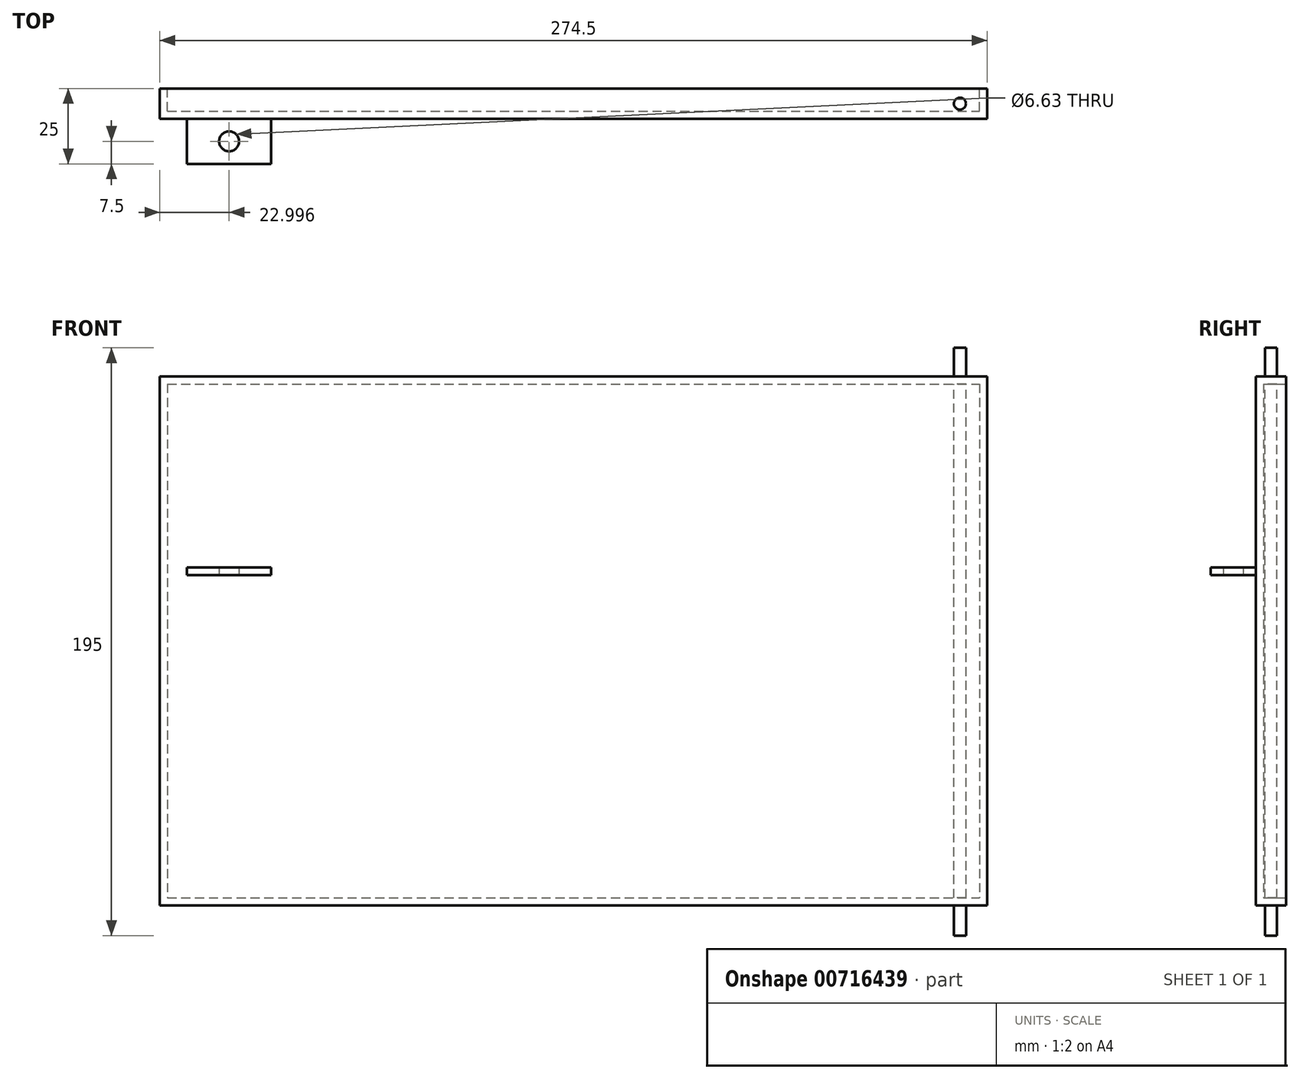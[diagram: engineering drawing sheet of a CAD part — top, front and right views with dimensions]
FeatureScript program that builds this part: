
annotation { "Feature Type Name" : "Feature", "Feature Type Description" : "" }
export const myFeature = defineFeature(function(context is Context, id is Id, definition is map)
    precondition{}
    {
        {
            var Q0;
            Q0=qCreatedBy(makeId("Top.planeOp"),FACE);
            var sketch = newSketch(context, id + "F0", { "sketchPlane" : qUnion([Q0])});
            skLineSegment(sketch, "E0.bottom", {"start": v(0, 0) * mm, "end": v(274.5, 0) * mm});
            skLineSegment(sketch, "E0.top", {"start": v(0, 10) * mm, "end": v(274.5, 10) * mm});
            skLineSegment(sketch, "E0.left", {"start": v(0, 0) * mm, "end": v(0, 10) * mm});
            skLineSegment(sketch, "E0.right", {"start": v(274.5, 0) * mm, "end": v(274.5, 10) * mm});
            skSolve(sketch);
        }
        {
            var Q0;
            Q0=qSketchRegion(id+"F0",true);
            extrude(context, id + "F1", {"entities" : qUnion([Q0]), "depth" : 175.5 * mm, "offsetDistance" : 25 * mm});
        }
        {
            var Q0;
            Q0=makeQuery(id+"F1.opExtrude","SWEPT_FACE",FACE,{"disambiguationData":[OSD([sQuery(id+"F0.wireOp",EDGE,"E0.top")])]});
            shell(context, id + "F2", {"entities" : qUnion([Q0]), "thickness" : 2.5 * mm});
        }
        {
            var Q0;
            Q0=makeQuery(id+"F1.opExtrude","CAP_FACE",FACE,{"disambiguationData":[OSD([sQuery(id+"F0.wireOp",EDGE,"E0.bottom"),sQuery(id+"F0.wireOp",EDGE,"E0.top"),sQuery(id+"F0.wireOp",EDGE,"E0.left"),sQuery(id+"F0.wireOp",EDGE,"E0.right")])],"isStart":true});
            var sketch = newSketch(context, id + "F3", { "sketchPlane" : qUnion([Q0])});
            skCircle(sketch, "E1", {"center": v(265.5, -5) * mm, "radius": 2 * mm});
            skPoint(sketch, "E1.centerSnap0", {"position": v(274.5, -5) * mm});
            skSolve(sketch);
        }
        {
            var Q0;
            Q0=qSketchRegion(id+"F3",true);
            extrude(context, id + "F4", {"entities" : qUnion([Q0]), "operationType" : NewBodyOperationType.ADD, "depth" : 10 * mm, "offsetDistance" : 25 * mm, "hasSecondDirection" : true, "secondDirectionOppositeDirection" : true, "secondDirectionDepth" : 185 * mm});
        }
        {
            var Q0;
            Q0=makeQuery(id+"F1.opExtrude","SWEPT_FACE",FACE,{"disambiguationData":[OSD([sQuery(id+"F0.wireOp",EDGE,"E0.bottom")])]});
            var sketch = newSketch(context, id + "F5", { "sketchPlane" : qUnion([Q0])});
            skLineSegment(sketch, "E2.bottom", {"start": v(9.05, 109.64) * mm, "end": v(36.95, 109.64) * mm});
            skLineSegment(sketch, "E2.top", {"start": v(9.05, 112.07) * mm, "end": v(36.95, 112.07) * mm});
            skLineSegment(sketch, "E2.left", {"start": v(9.05, 109.64) * mm, "end": v(9.05, 112.07) * mm});
            skLineSegment(sketch, "E2.right", {"start": v(36.95, 109.64) * mm, "end": v(36.95, 112.07) * mm});
            skSolve(sketch);
        }
        {
            var Q0;
            Q0=qSketchRegion(id+"F5",true);
            extrude(context, id + "F6", {"entities" : qUnion([Q0]), "operationType" : NewBodyOperationType.ADD, "depth" : 15 * mm, "offsetDistance" : 25 * mm});
        }
        {
            var Q0;
            Q0=makeQuery(id+"F6.opExtrude","SWEPT_FACE",FACE,{"disambiguationData":[OSD([sQuery(id+"F5.wireOp",EDGE,"E2.bottom")])]});
            var sketch = newSketch(context, id + "F7", { "sketchPlane" : qUnion([Q0])});
            skCircle(sketch, "E3", {"center": v(23, 7.5) * mm, "radius": 3.31 * mm});
            skPoint(sketch, "E3.centerSnap0", {"position": v(23, 15) * mm});
            skPoint(sketch, "E3.centerSnap1", {"position": v(9.05, 7.5) * mm});
            skSolve(sketch);
        }
        {
            var Q0;
            Q0=qSketchRegion(id+"F7",true);
            extrude(context, id + "F8", {"entities" : qUnion([Q0]), "operationType" : NewBodyOperationType.REMOVE, "oppositeDirection" : true, "depth" : 25 * mm, "offsetDistance" : 25 * mm});
        }
    });
